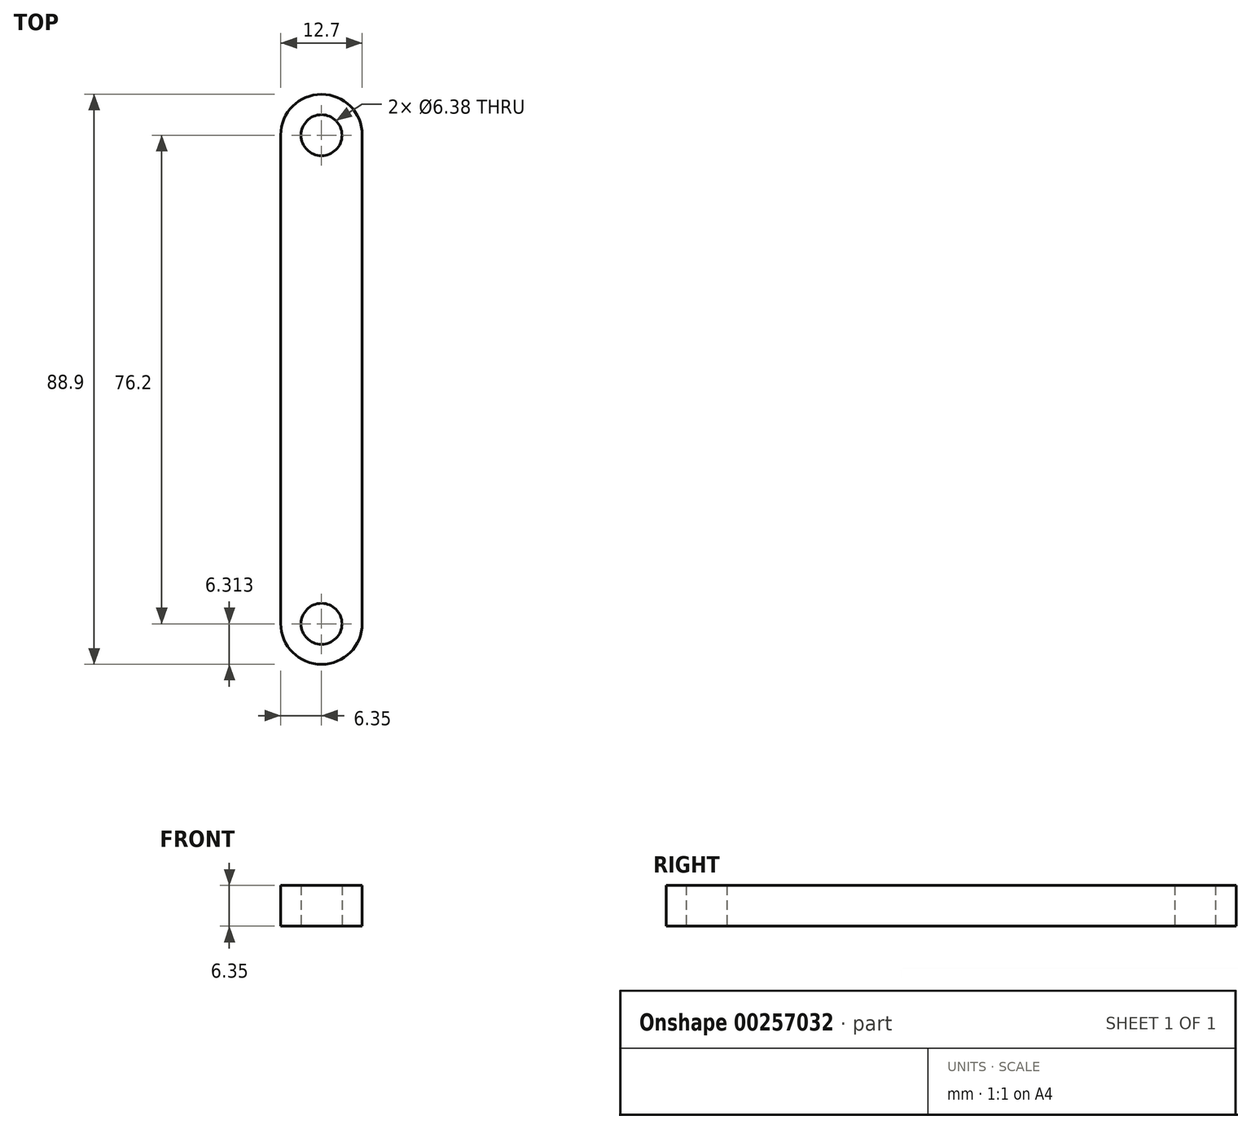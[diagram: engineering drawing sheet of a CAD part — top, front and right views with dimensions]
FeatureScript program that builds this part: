
annotation { "Feature Type Name" : "Feature", "Feature Type Description" : "" }
export const myFeature = defineFeature(function(context is Context, id is Id, definition is map)
    precondition{}
    {
        {
            var Q0;
            Q0=qCreatedBy(makeId("Top.planeOp"),FACE);
            var sketch = newSketch(context, id + "F0", { "sketchPlane" : qUnion([Q0])});
            skLineSegment(sketch, "E0.bottom", {"start": v(0, 44.45) * mm, "end": v(0, 44.45) * mm});
            skLineSegment(sketch, "E0.top", {"start": v(0, -44.45) * mm, "end": v(0, -44.45) * mm});
            skLineSegment(sketch, "E0.left", {"start": v(6.35, 38.1) * mm, "end": v(6.35, -38.1) * mm});
            skLineSegment(sketch, "E0.right", {"start": v(-6.35, 38.1) * mm, "end": v(-6.35, -38.1) * mm});
            skPoint(sketch, "E0.middle", {"position": v(0, 0) * mm});
            skCircle(sketch, "E1", {"center": v(0, 38.06) * mm, "radius": 3.19 * mm});
            skCircle(sketch, "E2", {"center": v(0, -38.14) * mm, "radius": 3.19 * mm});
            skArc(sketch, "E3.filletArc", {"start": v(0, 44.45) * mm, "mid": v(-4.5, 42.6) * mm, "end": v(-6.35, 38.1) * mm});
            skPoint(sketch, "E4.visualSharp", {"position": v(6.35, 44.45) * mm});
            skArc(sketch, "E4.filletArc", {"start": v(6.35, 38.1) * mm, "mid": v(4.5, 42.6) * mm, "end": v(0, 44.45) * mm});
            skPoint(sketch, "E5.visualSharp", {"position": v(-6.35, -44.45) * mm});
            skArc(sketch, "E5.filletArc", {"start": v(-6.35, -38.1) * mm, "mid": v(-4.5, -42.6) * mm, "end": v(0, -44.45) * mm});
            skPoint(sketch, "E6.visualSharp", {"position": v(6.35, -44.45) * mm});
            skArc(sketch, "E6.filletArc", {"start": v(0, -44.45) * mm, "mid": v(4.5, -42.6) * mm, "end": v(6.35, -38.1) * mm});
            skSolve(sketch);
        }
        {
            var Q0;
            Q0 = qSketchRegion(id + "F0", true);
            extrude(context, id + "F1", {"entities" : qUnion([Q0]), "depth" : 6.35 * mm});
        }
    });
